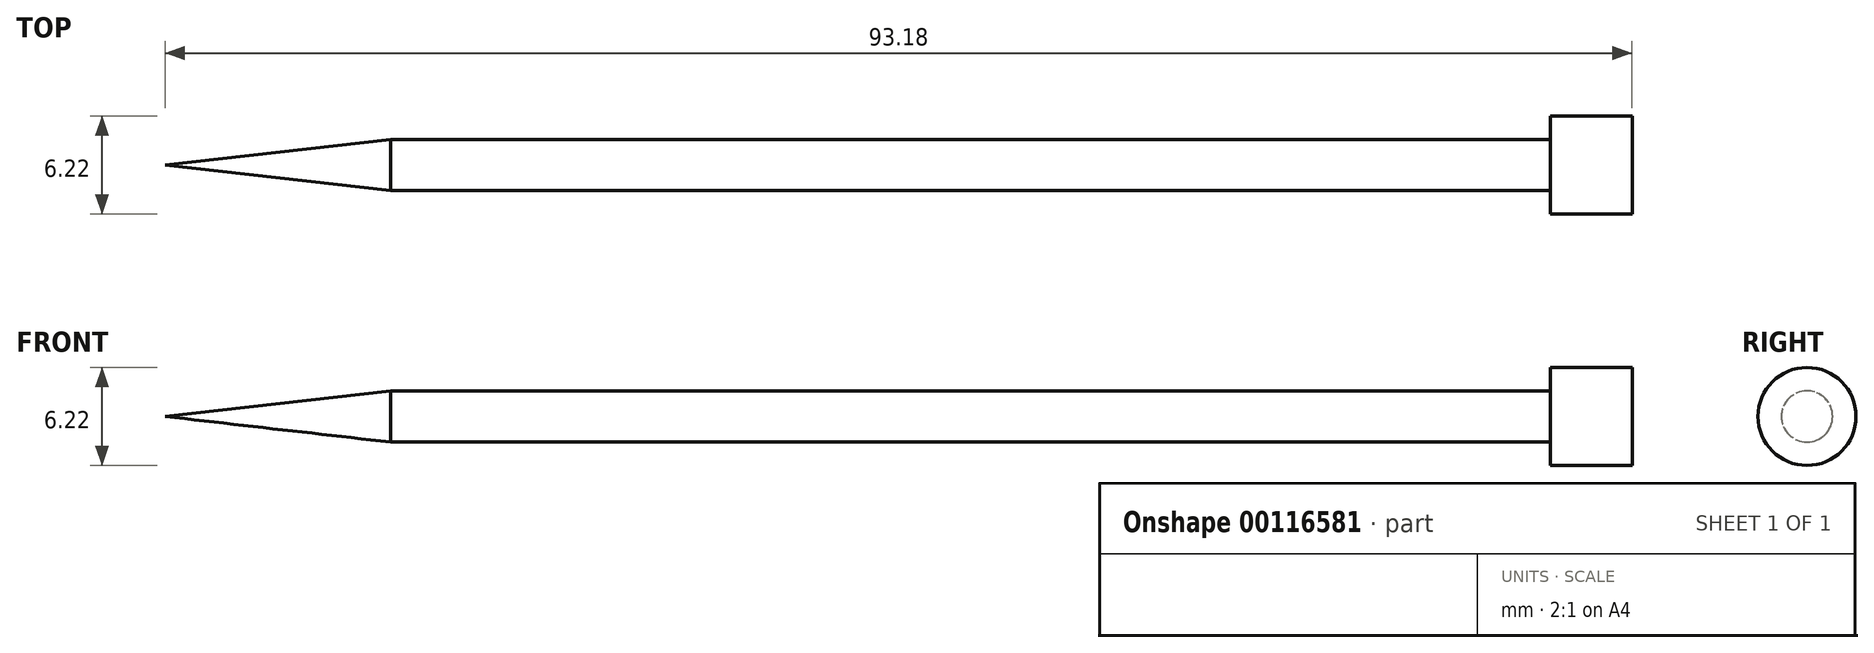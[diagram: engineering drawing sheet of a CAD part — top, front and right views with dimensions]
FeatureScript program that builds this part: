
annotation { "Feature Type Name" : "Feature", "Feature Type Description" : "" }
export const myFeature = defineFeature(function(context is Context, id is Id, definition is map)
    precondition{}
    {
        {
            var Q0;
            Q0=qCreatedBy(makeId("Front.planeOp"),FACE);
            var sketch = newSketch(context, id + "F0", { "sketchPlane" : qUnion([Q0])});
            skLineSegment(sketch, "E0.bottom", {"start": v(-37.62, 27.66) * mm, "end": v(36.04, 27.66) * mm});
            skLineSegment(sketch, "E1", {"start": v(-37.62, 27.66) * mm, "end": v(-51.94, 27.66) * mm});
            skLineSegment(sketch, "E2", {"start": v(-51.94, 27.66) * mm, "end": v(-37.62, 29.29) * mm});
            skLineSegment(sketch, "E3", {"start": v(-37.62, 29.29) * mm, "end": v(36.04, 29.29) * mm});
            skLineSegment(sketch, "E4", {"start": v(36.04, 29.29) * mm, "end": v(36.04, 27.66) * mm});
            skLineSegment(sketch, "E5.bottom", {"start": v(36.04, 27.66) * mm, "end": v(41.24, 27.66) * mm});
            skLineSegment(sketch, "E5.top", {"start": v(36.04, 30.77) * mm, "end": v(41.24, 30.77) * mm});
            skLineSegment(sketch, "E5.left", {"start": v(36.04, 27.66) * mm, "end": v(36.04, 30.77) * mm});
            skLineSegment(sketch, "E5.right", {"start": v(41.24, 27.66) * mm, "end": v(41.24, 30.77) * mm});
            skSolve(sketch);
        }
        {
            var Q0;
            {var subQ1=sQuery(id+"F0.wireOp",EDGE,"E0.bottom");Q0=makeQuery(id+"F0.imprint","IMPRINT",FACE,{"disambiguationData":[TD([[makeQuery(id+"F0.imprint","IMPRINT",EDGE,{"derivedFrom":subQ1}),1.0]])]});}
            var Q1;
            Q1=sQuery(id+"F0.wireOp",EDGE,"E0.bottom");
            revolve(context, id + "F1", {"entities" : qUnion([Q0]), "axis" : qUnion([Q1]), "revolveType" : RevolveType.FULL});
        }
        {
            var Q0;
            {var subQ3=sQuery(id+"F0.wireOp",EDGE,"E5.bottom");Q0=makeQuery(id+"F0.imprint","IMPRINT",FACE,{"disambiguationData":[TD([[makeQuery(id+"F0.imprint","IMPRINT",EDGE,{"derivedFrom":subQ3}),1.0]])]});}
            var Q1;
            Q1=sQuery(id+"F0.wireOp",EDGE,"E5.bottom");
            revolve(context, id + "F2", {"operationType" : NewBodyOperationType.ADD, "entities" : qUnion([Q0]), "axis" : qUnion([Q1]), "revolveType" : RevolveType.FULL});
        }
    });
